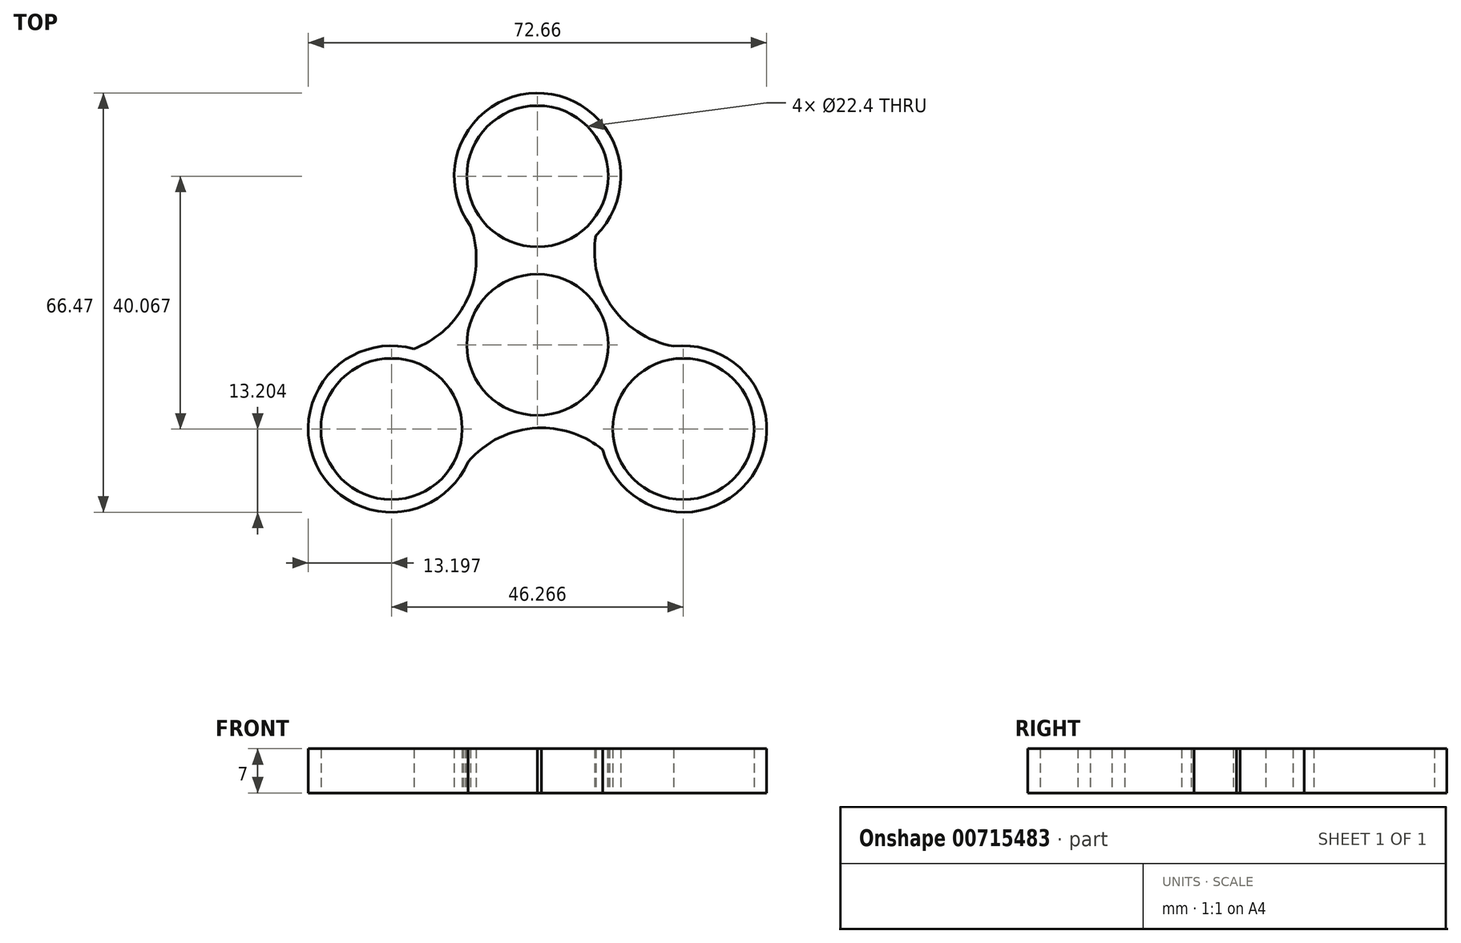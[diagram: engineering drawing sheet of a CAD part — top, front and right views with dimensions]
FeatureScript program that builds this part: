
annotation { "Feature Type Name" : "Feature", "Feature Type Description" : "" }
export const myFeature = defineFeature(function(context is Context, id is Id, definition is map)
    precondition{}
    {
        {
            var Q0;
            Q0=qCreatedBy(makeId("Top.planeOp"),FACE);
            var sketch = newSketch(context, id + "F0", { "sketchPlane" : qUnion([Q0])});
            skCircle(sketch, "E0", {"center": v(0, 0) * mm, "radius": 11.2 * mm});
            skArc(sketch, "E1", {"start": v(11.44, 6.58) * mm, "mid": v(11.28, 6.86) * mm, "end": v(11.1, 7.14) * mm});
            skCircle(sketch, "E2", {"center": v(0, 26.71) * mm, "radius": 11.2 * mm});
            skArc(sketch, "E3", {"start": v(9.24, 17.29) * mm, "mid": v(1.03, 39.87) * mm, "end": v(-10.6, 18.83) * mm});
            skArc(sketch, "E4.1.0", {"start": v(-19.59, -0.64) * mm, "mid": v(-35.04, -19.05) * mm, "end": v(-11.01, -18.59) * mm});
            skArc(sketch, "E4.2.0", {"start": v(10.35, -16.65) * mm, "mid": v(34.02, -20.83) * mm, "end": v(21.6, -0.24) * mm});
            skCircle(sketch, "E5.1.0", {"center": v(-23.13, -13.36) * mm, "radius": 11.2 * mm});
            skCircle(sketch, "E5.2.0", {"center": v(23.13, -13.36) * mm, "radius": 11.2 * mm});
            skArc(sketch, "E6", {"start": v(9.24, 17.29) * mm, "mid": v(11.84, 6) * mm, "end": v(21.6, -0.24) * mm});
            skArc(sketch, "E7.1.0", {"start": v(-19.59, -0.64) * mm, "mid": v(-11.1, 7.26) * mm, "end": v(-10.6, 18.83) * mm});
            skArc(sketch, "E7.2.0", {"start": v(10.35, -16.65) * mm, "mid": v(-0.73, -13.25) * mm, "end": v(-11.01, -18.59) * mm});
            skArc(sketch, "E8.trimOffspring", {"start": v(-11.42, 6.62) * mm, "mid": v(-11.58, 6.33) * mm, "end": v(-11.73, 6.05) * mm});
            skArc(sketch, "E9.trimOffspring", {"start": v(-0.02, -13.2) * mm, "mid": v(0.3, -13.2) * mm, "end": v(0.63, -13.18) * mm});
            skSolve(sketch);
        }
        {
            var Q0;
            Q0 = qSketchRegion(id + "F0", true);
            extrude(context, id + "F1", {"entities" : qUnion([Q0]), "depth" : 7 * mm, "offsetDistance" : 25 * mm});
        }
    });
